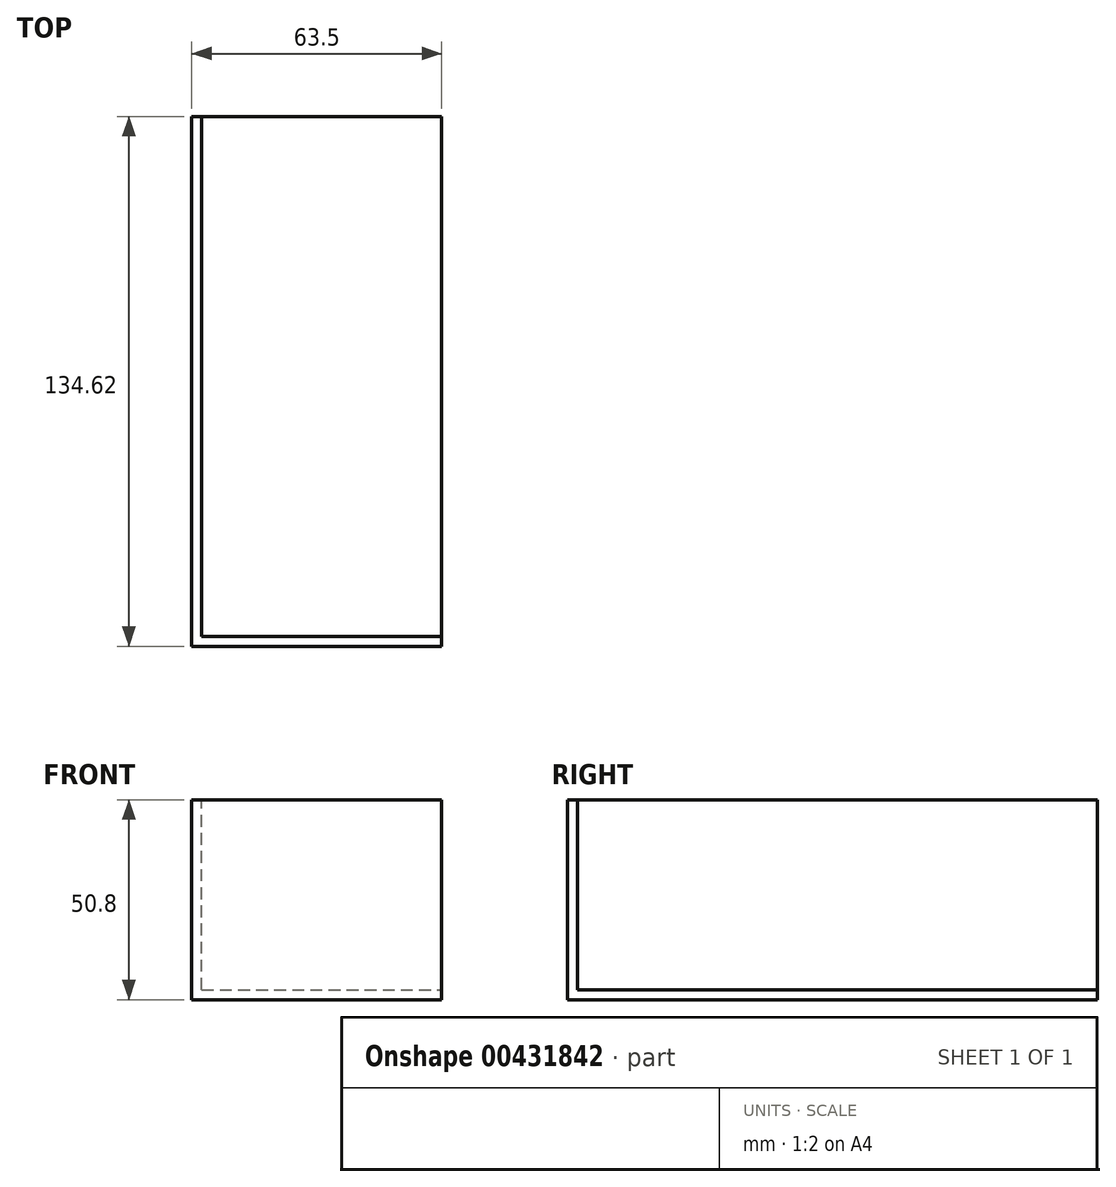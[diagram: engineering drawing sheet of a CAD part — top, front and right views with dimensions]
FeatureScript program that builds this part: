
annotation { "Feature Type Name" : "Feature", "Feature Type Description" : "" }
export const myFeature = defineFeature(function(context is Context, id is Id, definition is map)
    precondition{}
    {
        {
            var Q0;
            Q0=qCreatedBy(makeId("Front.planeOp"),FACE);
            var sketch = newSketch(context, id + "F0", { "sketchPlane" : qUnion([Q0])});
            skLineSegment(sketch, "E0.bottom", {"start": v(-31.75, -25.4) * mm, "end": v(31.75, -25.4) * mm});
            skLineSegment(sketch, "E0.top", {"start": v(-31.75, 25.4) * mm, "end": v(31.75, 25.4) * mm});
            skLineSegment(sketch, "E0.left", {"start": v(-31.75, -25.4) * mm, "end": v(-31.75, 25.4) * mm});
            skLineSegment(sketch, "E0.right", {"start": v(31.75, -25.4) * mm, "end": v(31.75, 25.4) * mm});
            skPoint(sketch, "E0.middle", {"position": v(0, 0) * mm});
            skSolve(sketch);
        }
        {
            var Q0;
            Q0=makeQuery(id+"F0.imprint","IMPRINT",FACE,{"disambiguationData":[TD([[makeQuery(id+"F0.imprint","IMPRINT",EDGE,{"derivedFrom":sQuery(id+"F0.wireOp",EDGE,"E0.bottom")}),1.0]])]});
            extrude(context, id + "F1", {"entities" : qUnion([Q0]), "depth" : 134.62 * mm});
        }
        {
            var Q0;
            Q0=makeQuery(id+"F1.opExtrude","SWEPT_FACE",FACE,{"disambiguationData":[OSD([sQuery(id+"F0.wireOp",EDGE,"E0.top")])]});
            var Q1;
            Q1=makeQuery(id+"F1.opExtrude","SWEPT_FACE",FACE,{"disambiguationData":[OSD([sQuery(id+"F0.wireOp",EDGE,"E0.right")])]});
            var Q2;
            Q2=makeQuery(id+"F1.opExtrude","CAP_FACE",FACE,{"disambiguationData":[OSD([sQuery(id+"F0.wireOp",EDGE,"E0.bottom"),sQuery(id+"F0.wireOp",EDGE,"E0.top"),sQuery(id+"F0.wireOp",EDGE,"E0.left"),sQuery(id+"F0.wireOp",EDGE,"E0.right")])],"isStart":true});
            shell(context, id + "F2", {"entities" : qUnion([Q0, Q1, Q2]), "thickness" : 2.54 * mm});
        }
    });
